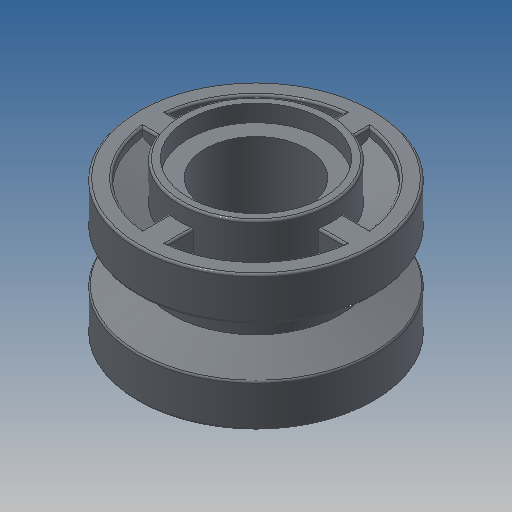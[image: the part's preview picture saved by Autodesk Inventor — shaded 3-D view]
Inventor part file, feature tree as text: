
AUTODESK INVENTOR PART (.ipt)
format: ipt  version: 2022.2 (Build 262287000, 287)  size: 430,080 bytes
history: native  units: in
note: dims shown in document units (in); Inventor stores cm internally (conversion verified against a paired STEP export)
features: sketch x2, revolve x1, extrude x1, mirror x1, fillet x1
ambient origin geometry x8: Origin, YZ Plane, XZ Plane, XY Plane, X Axis, Y Axis, Z Axis, Center Point
bodies: Solid1 (feature_tree)
feature tree (6):
  revolve  "Revolution1"  [1 undecoded]
  extrude  "Extrusion1"  Depth=0.0039in
  mirror  "Mirror1"
  fillet  "Fillet1"  Radius=0.2835in
  sketch  "Sketch2"  dims[d0=0.189in d1=0.252in]
  sketch  "Sketch3"  dims[d2=0.0315in d3=0.315in d4=0.2835in d5=0.4409in d6=0.378in d7=0.252in d8=0.0315in d9=0.315in d10=0.0157in d11=0.0945in d12=90.0deg d14=0.0472in d15=0.3937in d16=0.0in d17=0.0039in]
note: 1 required parameter value undecoded (feature->parameter linkage not recoverable at this tier; creation-order binding heuristic only, values carry confidence <= 0.55)
